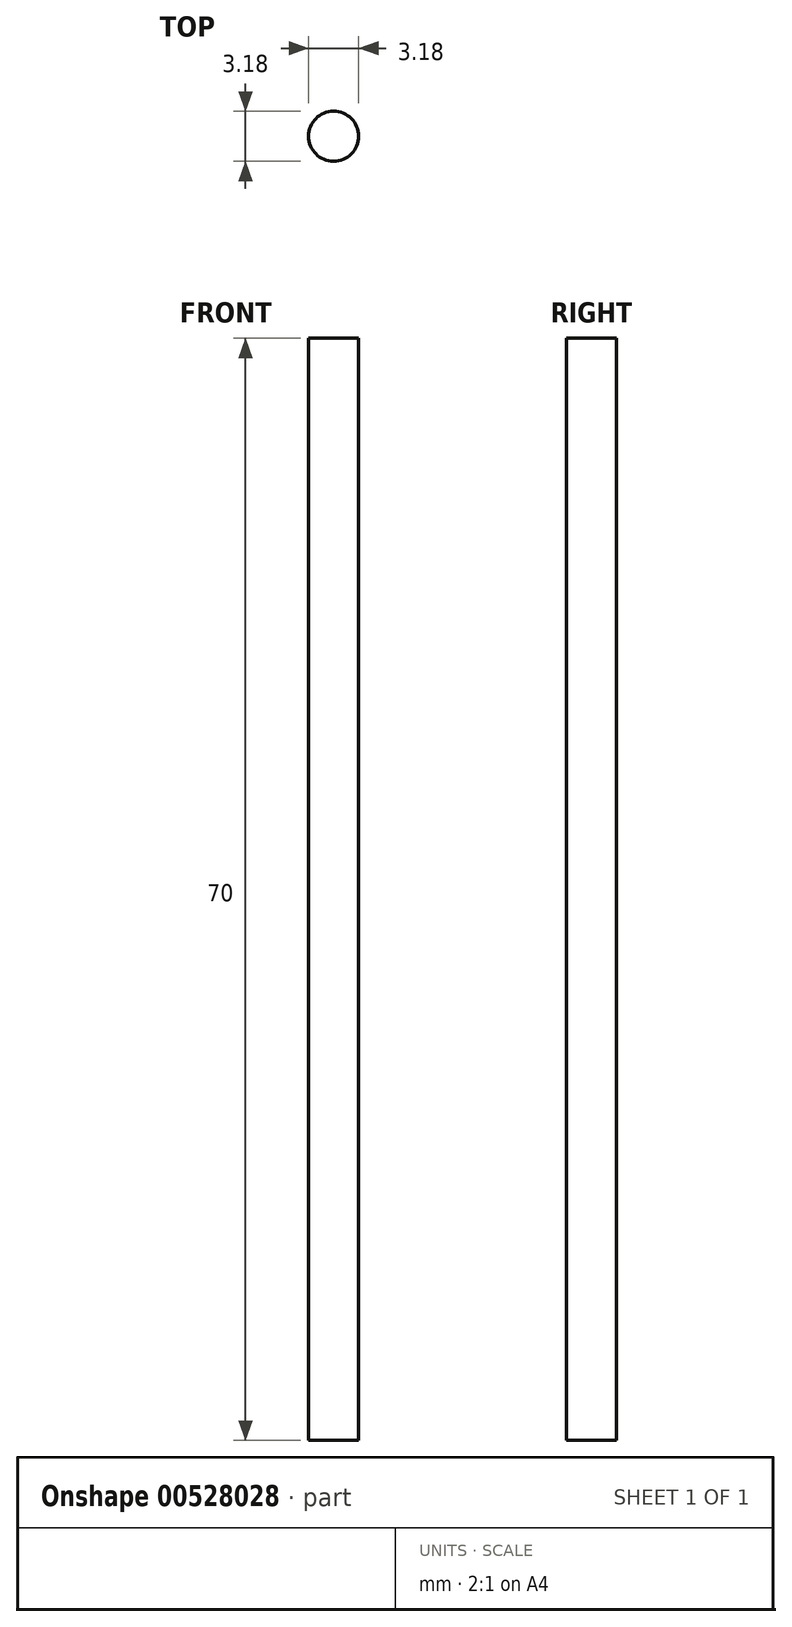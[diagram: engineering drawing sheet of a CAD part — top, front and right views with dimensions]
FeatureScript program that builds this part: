
annotation { "Feature Type Name" : "Feature", "Feature Type Description" : "" }
export const myFeature = defineFeature(function(context is Context, id is Id, definition is map)
    precondition{}
    {
        {
            var Q0;
            Q0=qCreatedBy(makeId("Top.planeOp"),FACE);
            var sketch = newSketch(context, id + "F0", { "sketchPlane" : qUnion([Q0])});
            skCircle(sketch, "E0", {"center": v(0, 0) * mm, "radius": 1.59 * mm});
            skSolve(sketch);
        }
        {
            var Q0;
            Q0=makeQuery(id+"F0.imprint","IMPRINT",FACE,{"disambiguationData":[TD([[makeQuery(id+"F0.imprint","IMPRINT",EDGE,{"derivedFrom":sQuery(id+"F0.wireOp",EDGE,"E0")}),1.0]])]});
            extrude(context, id + "F1", {"entities" : qUnion([Q0]), "depth" : 70 * mm, "offsetDistance" : 25 * mm});
        }
    });
